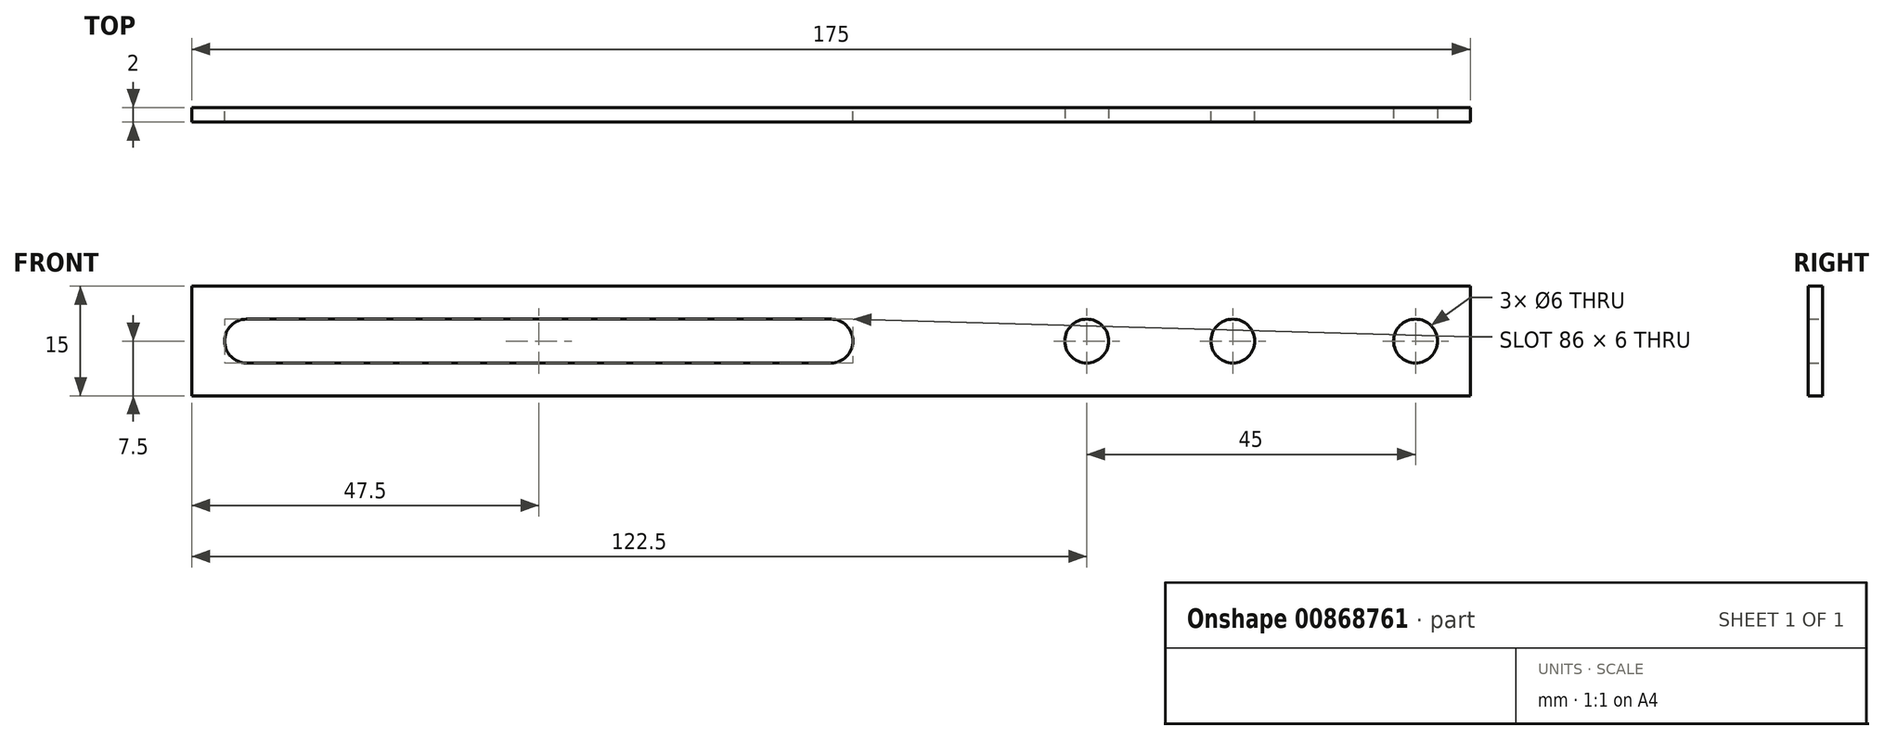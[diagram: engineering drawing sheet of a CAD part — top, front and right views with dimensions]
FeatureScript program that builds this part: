
annotation { "Feature Type Name" : "Feature", "Feature Type Description" : "" }
export const myFeature = defineFeature(function(context is Context, id is Id, definition is map)
    precondition{}
    {
        {
            var Q0;
            Q0=qCreatedBy(makeId("Front.planeOp"),FACE);
            var sketch = newSketch(context, id + "F0", { "sketchPlane" : qUnion([Q0])});
            skArc(sketch, "E0", {"start": v(0, 3) * mm, "mid": v(-3, 0) * mm, "end": v(0, -3) * mm});
            skLineSegment(sketch, "E1.bottom", {"start": v(-7.5, -7.5) * mm, "end": v(142.5, -7.5) * mm});
            skLineSegment(sketch, "E1.top", {"start": v(-7.5, 7.5) * mm, "end": v(142.5, 7.5) * mm});
            skLineSegment(sketch, "E1.left", {"start": v(-7.5, -7.5) * mm, "end": v(-7.5, 7.5) * mm});
            skLineSegment(sketch, "E1.right", {"start": v(142.5, -7.5) * mm, "end": v(142.5, 7.5) * mm});
            skArc(sketch, "E2", {"start": v(135, -3) * mm, "mid": v(138, 0) * mm, "end": v(135, 3) * mm});
            skArc(sketch, "E3", {"start": v(135, -3) * mm, "mid": v(132, 0) * mm, "end": v(135, 3) * mm});
            skLineSegment(sketch, "E4.bottom", {"start": v(0, -3) * mm, "end": v(80, -3) * mm});
            skLineSegment(sketch, "E4.top", {"start": v(0, 3) * mm, "end": v(80, 3) * mm});
            skArc(sketch, "E5", {"start": v(80, 3) * mm, "mid": v(83, 0) * mm, "end": v(80, -3) * mm});
            skSolve(sketch);
        }
        {
            var Q0;
            Q0=makeQuery(id+"F0.imprint","IMPRINT",FACE,{"disambiguationData":[TD([[makeQuery(id+"F0.imprint","IMPRINT",EDGE,{"derivedFrom":sQuery(id+"F0.wireOp",EDGE,"E0")}),-1.0]])]});
            extrude(context, id + "F1", {"entities" : qUnion([Q0]), "depth" : 2 * mm, "offsetDistance" : 25 * mm, "symmetric" : true});
        }
        {
            var Q0;
            Q0=makeQuery(id+"F1.opExtrude","SWEPT_FACE",FACE,{"disambiguationData":[OSD([sQuery(id+"F0.wireOp",EDGE,"E1.right")])]});
            var sketch = newSketch(context, id + "F2", { "sketchPlane" : qUnion([Q0])});
            skLineSegment(sketch, "E6.0", {"start": v(-1, -7.5) * mm, "end": v(-1, 7.5) * mm});
            skLineSegment(sketch, "E7.0", {"start": v(1, -7.5) * mm, "end": v(1, 7.5) * mm});
            skLineSegment(sketch, "E8.0", {"start": v(-1, 7.5) * mm, "end": v(1, 7.5) * mm});
            skLineSegment(sketch, "E9.0", {"start": v(-1, -7.5) * mm, "end": v(1, -7.5) * mm});
            skSolve(sketch);
        }
        {
            var Q0;
            Q0=makeQuery(id+"F2.imprint","IMPRINT",FACE,{"disambiguationData":[TD([[makeQuery(id+"F2.imprint","IMPRINT",EDGE,{"derivedFrom":sQuery(id+"F2.wireOp",EDGE,"E6.0")}),-1.0]])]});
            extrude(context, id + "F3", {"entities" : qUnion([Q0]), "operationType" : NewBodyOperationType.ADD, "depth" : 25 * mm, "offsetDistance" : 25 * mm});
        }
        {
            var Q0;
            Q0=makeQuery(id+"F3.boolean.opBoolean","MERGE",FACE,{"derivedFrom":[makeQuery(id+"F1.opExtrude","CAP_FACE",FACE,{"disambiguationData":[OSD([sQuery(id+"F0.wireOp",EDGE,"E0"),sQuery(id+"F0.wireOp",EDGE,"E1.bottom"),sQuery(id+"F0.wireOp",EDGE,"E1.top"),sQuery(id+"F0.wireOp",EDGE,"E1.left"),sQuery(id+"F0.wireOp",EDGE,"E1.right"),sQuery(id+"F0.wireOp",EDGE,"E2"),sQuery(id+"F0.wireOp",EDGE,"E3"),sQuery(id+"F0.wireOp",EDGE,"E4.bottom"),sQuery(id+"F0.wireOp",EDGE,"E4.top"),sQuery(id+"F0.wireOp",EDGE,"E5")])],"isStart":false}),makeQuery(id+"F3.opExtrude","SWEPT_FACE",FACE,{"disambiguationData":[OSD([sQuery(id+"F2.wireOp",EDGE,"E6.0")])]})]});
            var sketch = newSketch(context, id + "F4", { "sketchPlane" : qUnion([Q0])});
            skCircle(sketch, "E10", {"center": v(160, 0) * mm, "radius": 3 * mm});
            skSolve(sketch);
        }
        {
            var Q0;
            Q0=makeQuery(id+"F4.imprint","IMPRINT",FACE,{"disambiguationData":[TD([[makeQuery(id+"F4.imprint","IMPRINT",EDGE,{"derivedFrom":sQuery(id+"F4.wireOp",EDGE,"E10")}),1.0]])]});
            extrude(context, id + "F5", {"entities" : qUnion([Q0]), "operationType" : NewBodyOperationType.REMOVE, "endBound" : BoundingType.THROUGH_ALL, "oppositeDirection" : true, "depth" : 25 * mm, "offsetDistance" : 25 * mm});
        }
        {
            var Q0;
            Q0=makeQuery(id+"F3.boolean.opBoolean","MERGE",FACE,{"derivedFrom":[makeQuery(id+"F1.opExtrude","CAP_FACE",FACE,{"disambiguationData":[OSD([sQuery(id+"F0.wireOp",EDGE,"E0"),sQuery(id+"F0.wireOp",EDGE,"E1.bottom"),sQuery(id+"F0.wireOp",EDGE,"E1.top"),sQuery(id+"F0.wireOp",EDGE,"E1.left"),sQuery(id+"F0.wireOp",EDGE,"E1.right"),sQuery(id+"F0.wireOp",EDGE,"E2"),sQuery(id+"F0.wireOp",EDGE,"E3"),sQuery(id+"F0.wireOp",EDGE,"E4.bottom"),sQuery(id+"F0.wireOp",EDGE,"E4.top"),sQuery(id+"F0.wireOp",EDGE,"E5")])],"isStart":false}),makeQuery(id+"F3.opExtrude","SWEPT_FACE",FACE,{"disambiguationData":[OSD([sQuery(id+"F2.wireOp",EDGE,"E6.0")])]})]});
            var sketch = newSketch(context, id + "F6", { "sketchPlane" : qUnion([Q0])});
            skCircle(sketch, "E11", {"center": v(115, 0) * mm, "radius": 3 * mm});
            skCircle(sketch, "E12.0", {"center": v(135, 0) * mm, "radius": 3 * mm, "construction": true});
            skSolve(sketch);
        }
        {
            var Q0;
            Q0=makeQuery(id+"F6.imprint","IMPRINT",FACE,{"disambiguationData":[TD([[makeQuery(id+"F6.imprint","IMPRINT",EDGE,{"derivedFrom":sQuery(id+"F6.wireOp",EDGE,"E11")}),1.0]])]});
            extrude(context, id + "F7", {"entities" : qUnion([Q0]), "operationType" : NewBodyOperationType.REMOVE, "endBound" : BoundingType.THROUGH_ALL, "oppositeDirection" : true, "depth" : 25 * mm, "offsetDistance" : 25 * mm});
        }
    });
